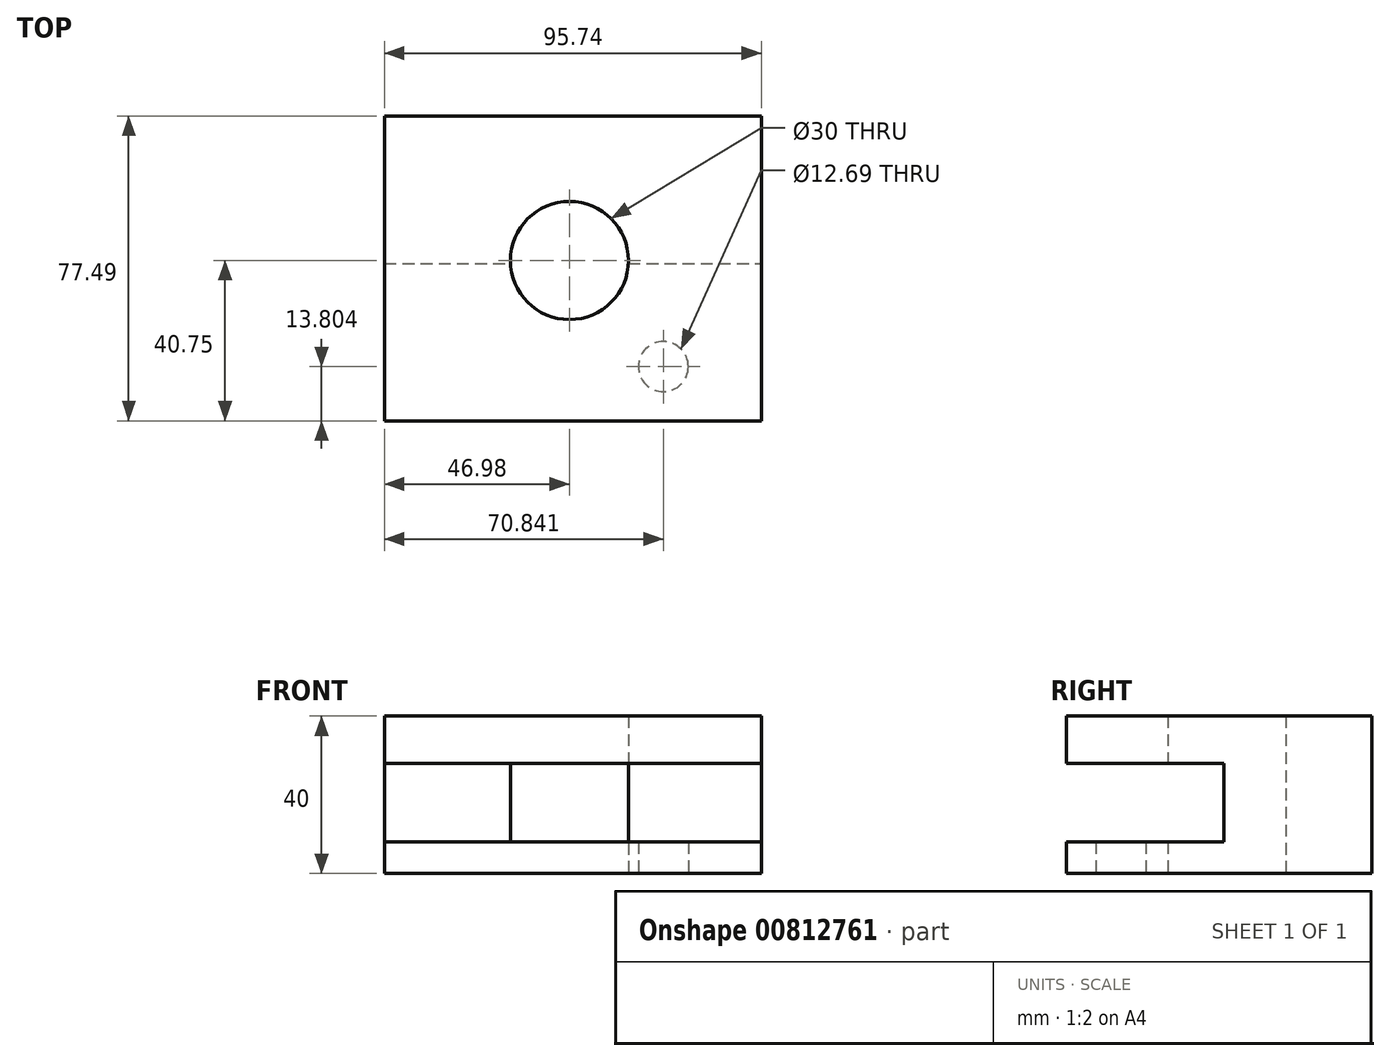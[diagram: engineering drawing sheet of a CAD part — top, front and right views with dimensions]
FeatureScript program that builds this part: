
annotation { "Feature Type Name" : "Feature", "Feature Type Description" : "" }
export const myFeature = defineFeature(function(context is Context, id is Id, definition is map)
    precondition{}
    {
        {
            var Q0;
            Q0=qCreatedBy(makeId("Top.planeOp"),FACE);
            var sketch = newSketch(context, id + "F0", { "sketchPlane" : qUnion([Q0])});
            skLineSegment(sketch, "E0.bottom", {"start": v(-46.98, 36.74) * mm, "end": v(48.76, 36.74) * mm});
            skLineSegment(sketch, "E0.top", {"start": v(-46.98, -40.75) * mm, "end": v(48.76, -40.75) * mm});
            skLineSegment(sketch, "E0.left", {"start": v(-46.98, 36.74) * mm, "end": v(-46.98, -40.75) * mm});
            skLineSegment(sketch, "E0.right", {"start": v(48.76, 36.74) * mm, "end": v(48.76, -40.75) * mm});
            skCircle(sketch, "E1", {"center": v(0, 0) * mm, "radius": 15 * mm});
            skSolve(sketch);
        }
        {
            var Q0;
            Q0=makeQuery(id+"F0.imprint","IMPRINT",FACE,{"disambiguationData":[TD([[makeQuery(id+"F0.imprint","IMPRINT",EDGE,{"derivedFrom":sQuery(id+"F0.wireOp",EDGE,"E0.bottom")}),-1.0]])]});
            extrude(context, id + "F1", {"entities" : qUnion([Q0]), "depth" : 40 * mm, "offsetDistance" : 25 * mm});
        }
        {
            var Q0;
            Q0=makeQuery(id+"F1.opExtrude","SWEPT_FACE",FACE,{"disambiguationData":[OSD([sQuery(id+"F0.wireOp",EDGE,"E0.top")])]});
            var sketch = newSketch(context, id + "F2", { "sketchPlane" : qUnion([Q0])});
            skLineSegment(sketch, "E2.bottom", {"start": v(-58, 27.99) * mm, "end": v(62, 27.99) * mm});
            skLineSegment(sketch, "E2.top", {"start": v(-58, 7.99) * mm, "end": v(62, 7.99) * mm});
            skLineSegment(sketch, "E2.left", {"start": v(-58, 27.99) * mm, "end": v(-58, 7.99) * mm});
            skLineSegment(sketch, "E2.right", {"start": v(62, 27.99) * mm, "end": v(62, 7.99) * mm});
            skSolve(sketch);
        }
        {
            var Q0;
            {var subQ0=sQuery(id+"F2.wireOp",EDGE,"E2.bottom");var subQ1=sQuery(id+"F0.wireOp",EDGE,"E0.top");var subQ2=makeQuery(id+"F1.opExtrude","SWEPT_EDGE",EDGE,{"disambiguationData":[OSD([subQ1,sQuery(id+"F0.wireOp",EDGE,"E0.left")])]});var subQ3=makeQuery(id+"F2.imprint","INTERSECT",VERTEX,{"derivedFrom":[subQ2,subQ0]});Q0=makeQuery(id+"F2.imprint","IMPRINT",FACE,{"disambiguationData":[TD([[makeQuery(id+"F2.imprint","IMPRINT",EDGE,{"disambiguationData":[TD([[subQ3,-1.0]])],"derivedFrom":subQ0}),-1.0]])]});}
            extrude(context, id + "F3", {"entities" : qUnion([Q0]), "operationType" : NewBodyOperationType.REMOVE, "oppositeDirection" : true, "depth" : 40 * mm, "offsetDistance" : 25 * mm});
        }
        {
            var Q0;
            Q0=makeQuery(id+"F1.opExtrude","CAP_FACE",FACE,{"disambiguationData":[OSD([sQuery(id+"F0.wireOp",EDGE,"E0.bottom"),sQuery(id+"F0.wireOp",EDGE,"E0.top"),sQuery(id+"F0.wireOp",EDGE,"E0.left"),sQuery(id+"F0.wireOp",EDGE,"E0.right"),sQuery(id+"F0.wireOp",EDGE,"E1")])],"isStart":true});
            var sketch = newSketch(context, id + "F4", { "sketchPlane" : qUnion([Q0])});
            skCircle(sketch, "E3", {"center": v(23.86, 26.95) * mm, "radius": 6.35 * mm});
            skSolve(sketch);
        }
        {
            var Q0;
            Q0=makeQuery(id+"F4.imprint","IMPRINT",FACE,{"disambiguationData":[TD([[makeQuery(id+"F4.imprint","IMPRINT",EDGE,{"derivedFrom":sQuery(id+"F4.wireOp",EDGE,"E3")}),1.0]])]});
            extrude(context, id + "F5", {"entities" : qUnion([Q0]), "operationType" : NewBodyOperationType.REMOVE, "oppositeDirection" : true, "depth" : 25 * mm, "offsetDistance" : 25 * mm});
        }
    });
